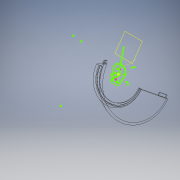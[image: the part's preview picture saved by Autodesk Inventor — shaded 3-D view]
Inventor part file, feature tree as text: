
AUTODESK INVENTOR PART (.ipt)
format: ipt  version: 2018 (Build 220112000, 112)  size: 246,272 bytes
history: native  units: mm
features: sketch x7, plane x3, revolve x1, extrude x1
ambient origin geometry x8: Origin, YZ Plane, XZ Plane, XY Plane, X Axis, Y Axis, Z Axis, Center Point
bodies: Body1 (feature_tree)
feature tree (12):
  sketch  "Sketch68"  dims[d600=2.7mm d601=1.4mm]
  sketch  "Sketch184"  dims[d603=1.265mm d605=180.0deg]
  plane  "Work Plane13"
  sketch  "Sketch199"  dims[d606=8.0mm]
  plane  "Work Plane14"
  sketch  "Sketch200"  dims[d625=90.0deg]
  plane  "Work Plane15"
  sketch  "Sketch201"  dims[d626=0.7mm]
  revolve  "Revolution6"  [1 undecoded]
  extrude  "Extrusion162"  TaperAngle=180.0deg  [1 undecoded]
  sketch  "Sketch213"  dims[d630=1.3mm]
  sketch  "Sketch214"  dims[d635=0.7mm d637=1.85mm d638=3.0mm d639=0.0mm d21=1.0mm d22=1.0mm]
note: 2 required parameter values undecoded (feature->parameter linkage not recoverable at this tier; creation-order binding heuristic only, values carry confidence <= 0.55)